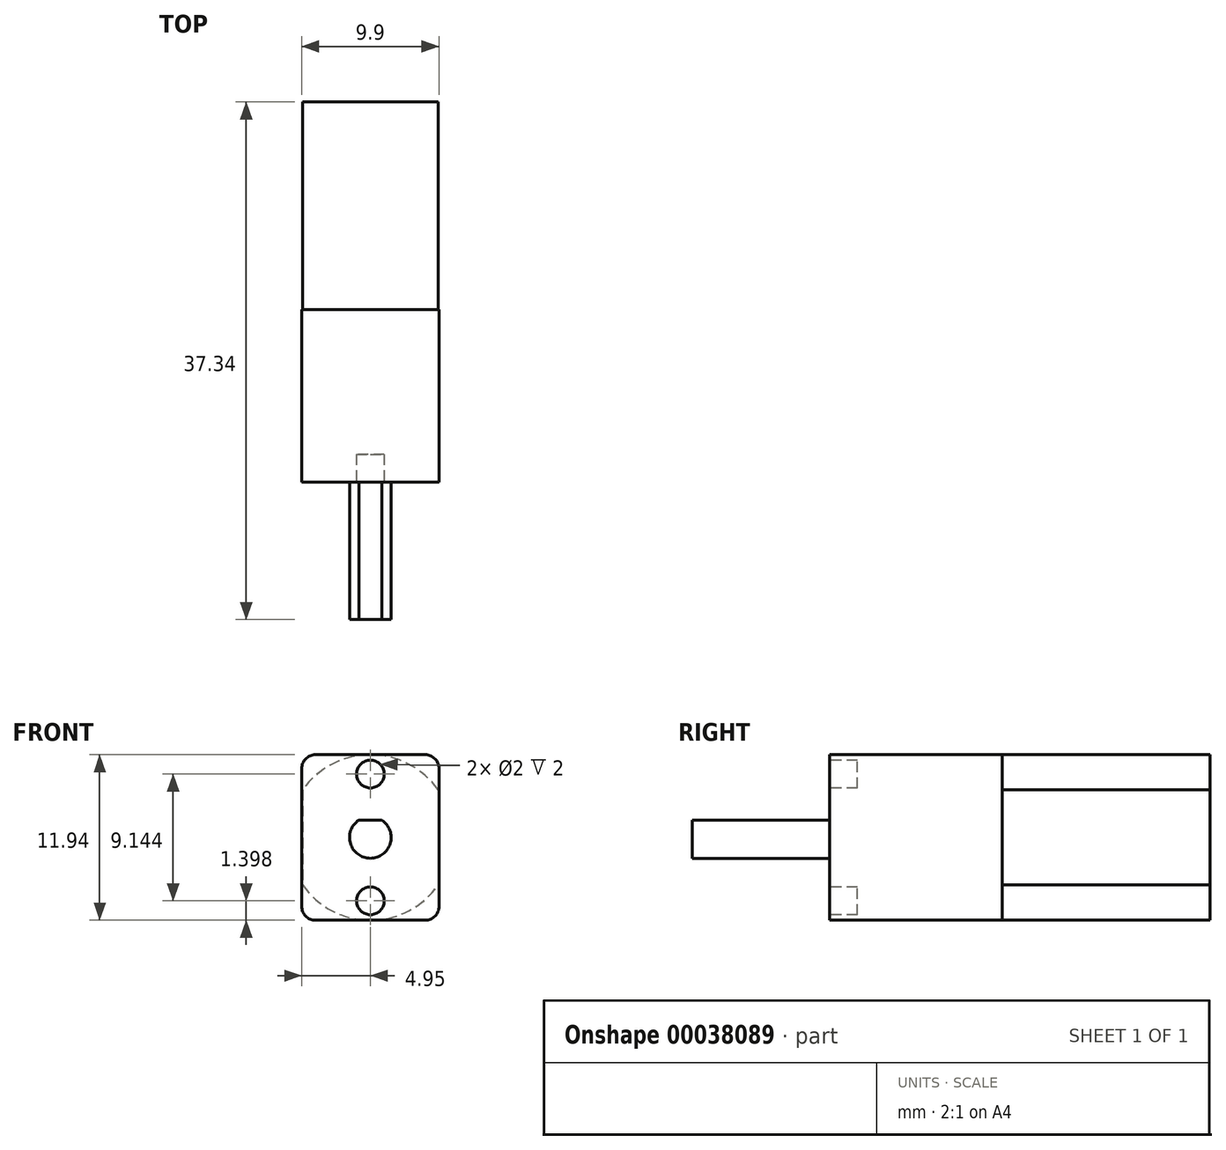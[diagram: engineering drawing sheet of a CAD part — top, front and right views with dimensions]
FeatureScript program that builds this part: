
annotation { "Feature Type Name" : "Feature", "Feature Type Description" : "" }
export const myFeature = defineFeature(function(context is Context, id is Id, definition is map)
    precondition{}
    {
        {
            var Q0;
            Q0=qCreatedBy(makeId("Front.planeOp"),FACE);
            var sketch = newSketch(context, id + "F0", { "sketchPlane" : qUnion([Q0])});
            skLineSegment(sketch, "E0.rect.bottom", {"start": v(-4.89, 3.43) * mm, "end": v(4.89, 3.43) * mm});
            skLineSegment(sketch, "E0.rect.top", {"start": v(-4.89, -3.43) * mm, "end": v(4.89, -3.43) * mm});
            skLineSegment(sketch, "E0.rect.left", {"start": v(-4.89, 3.43) * mm, "end": v(-4.89, -3.43) * mm});
            skLineSegment(sketch, "E0.rect.right", {"start": v(4.89, 3.43) * mm, "end": v(4.89, -3.43) * mm});
            skPoint(sketch, "E0.rect.middle", {"position": v(0, 0) * mm});
            skArc(sketch, "E1", {"start": v(-4.89, -3.43) * mm, "mid": v(0, -5.97) * mm, "end": v(4.89, -3.43) * mm});
            skArc(sketch, "E2", {"start": v(4.89, 3.43) * mm, "mid": v(0, 5.97) * mm, "end": v(-4.89, 3.43) * mm});
            skSolve(sketch);
        }
        {
            var Q0;
            Q0 = qSketchRegion(id + "F0", true);
            extrude(context, id + "F1", {"entities" : qUnion([Q0]), "depth" : 15 * mm});
        }
        {
            var Q0;
            Q0=makeQuery(id+"F1.opExtrude","CAP_FACE",FACE,{"disambiguationData":[OSD([sQuery(id+"F0.wireOp",EDGE,"E0.rect.left"),sQuery(id+"F0.wireOp",EDGE,"E0.rect.right"),sQuery(id+"F0.wireOp",EDGE,"E1"),sQuery(id+"F0.wireOp",EDGE,"E2")])],"isStart":false});
            var sketch = newSketch(context, id + "F2", { "sketchPlane" : qUnion([Q0])});
            skLineSegment(sketch, "E3.rect.bottom", {"start": v(-4.95, 5.97) * mm, "end": v(4.95, 5.97) * mm});
            skLineSegment(sketch, "E3.rect.top", {"start": v(-4.95, -5.97) * mm, "end": v(4.95, -5.97) * mm});
            skLineSegment(sketch, "E3.rect.left", {"start": v(-4.95, 5.97) * mm, "end": v(-4.95, -5.97) * mm});
            skLineSegment(sketch, "E3.rect.right", {"start": v(4.95, 5.97) * mm, "end": v(4.95, -5.97) * mm});
            skPoint(sketch, "E3.rect.middle", {"position": v(0, 0) * mm});
            skSolve(sketch);
        }
        {
            var Q0;
            Q0 = qSketchRegion(id + "F2", true);
            extrude(context, id + "F3", {"entities" : qUnion([Q0]), "operationType" : NewBodyOperationType.ADD, "depth" : 12.45 * mm});
        }
        {
            var Q0;
            Q0=makeQuery(id+"F3.opExtrude","CAP_FACE",FACE,{"disambiguationData":[OSD([sQuery(id+"F2.wireOp",EDGE,"E3.rect.bottom"),sQuery(id+"F2.wireOp",EDGE,"E3.rect.top"),sQuery(id+"F2.wireOp",EDGE,"E3.rect.left"),sQuery(id+"F2.wireOp",EDGE,"E3.rect.right")])],"isStart":false});
            var sketch = newSketch(context, id + "F4", { "sketchPlane" : qUnion([Q0])});
            skLineSegment(sketch, "E4", {"start": v(4.95, 0) * mm, "end": v(-4.95, 0) * mm, "construction": true});
            skPoint(sketch, "E5", {"position": v(0, 0) * mm});
            skLineSegment(sketch, "E6", {"start": v(0, -4.57) * mm, "end": v(0, 4.57) * mm, "construction": true});
            skCircle(sketch, "E7", {"center": v(0, -4.57) * mm, "radius": 1 * mm});
            skCircle(sketch, "E8", {"center": v(0, 4.57) * mm, "radius": 1 * mm});
            skSolve(sketch);
        }
        {
            var Q0;
            Q0 = qSketchRegion(id + "F4", true);
            extrude(context, id + "F5", {"entities" : qUnion([Q0]), "operationType" : NewBodyOperationType.REMOVE, "oppositeDirection" : true, "depth" : 2 * mm});
        }
        {
            var Q0;
            Q0=makeQuery(id+"F3.opExtrude","SWEPT_EDGE",EDGE,{"disambiguationData":[OSD([sQuery(id+"F2.wireOp",EDGE,"E3.rect.bottom"),sQuery(id+"F2.wireOp",EDGE,"E3.rect.left")])]});
            var Q1;
            Q1=makeQuery(id+"F3.opExtrude","SWEPT_EDGE",EDGE,{"disambiguationData":[OSD([sQuery(id+"F2.wireOp",EDGE,"E3.rect.bottom"),sQuery(id+"F2.wireOp",EDGE,"E3.rect.right")])]});
            var Q2;
            Q2=makeQuery(id+"F3.opExtrude","SWEPT_EDGE",EDGE,{"disambiguationData":[OSD([sQuery(id+"F2.wireOp",EDGE,"E3.rect.top"),sQuery(id+"F2.wireOp",EDGE,"E3.rect.right")])]});
            var Q3;
            Q3=makeQuery(id+"F3.opExtrude","SWEPT_EDGE",EDGE,{"disambiguationData":[OSD([sQuery(id+"F2.wireOp",EDGE,"E3.rect.top"),sQuery(id+"F2.wireOp",EDGE,"E3.rect.left")])]});
            fillet(context, id + "F6", {"entities" : qUnion([Q0, Q1, Q2, Q3]), "radius" : 1 * mm, "tangentPropagation" : true, "allowEdgeOverflow" : false});
        }
        {
            var Q0;
            Q0=makeQuery(id+"F3.opExtrude","CAP_FACE",FACE,{"disambiguationData":[OSD([sQuery(id+"F2.wireOp",EDGE,"E3.rect.bottom"),sQuery(id+"F2.wireOp",EDGE,"E3.rect.top"),sQuery(id+"F2.wireOp",EDGE,"E3.rect.left"),sQuery(id+"F2.wireOp",EDGE,"E3.rect.right")])],"isStart":false});
            var sketch = newSketch(context, id + "F7", { "sketchPlane" : qUnion([Q0])});
            skLineSegment(sketch, "E9", {"start": v(-4.95, 0) * mm, "end": v(4.95, 0) * mm, "construction": true});
            skCircle(sketch, "E10", {"center": v(0, 0) * mm, "radius": 1.5 * mm});
            skLineSegment(sketch, "E11", {"start": v(0.84, 1.25) * mm, "end": v(-0.84, 1.25) * mm});
            skSolve(sketch);
        }
        {
            var Q0;
            {var subQ0=sQuery(id+"F7.wireOp",EDGE,"E11");Q0=makeQuery(id+"F7.imprint","IMPRINT",FACE,{"disambiguationData":[TD([[makeQuery(id+"F7.imprint","IMPRINT",EDGE,{"derivedFrom":subQ0}),1.0]])]});}
            extrude(context, id + "F8", {"entities" : qUnion([Q0]), "operationType" : NewBodyOperationType.ADD, "depth" : 9.9 * mm});
        }
    });
